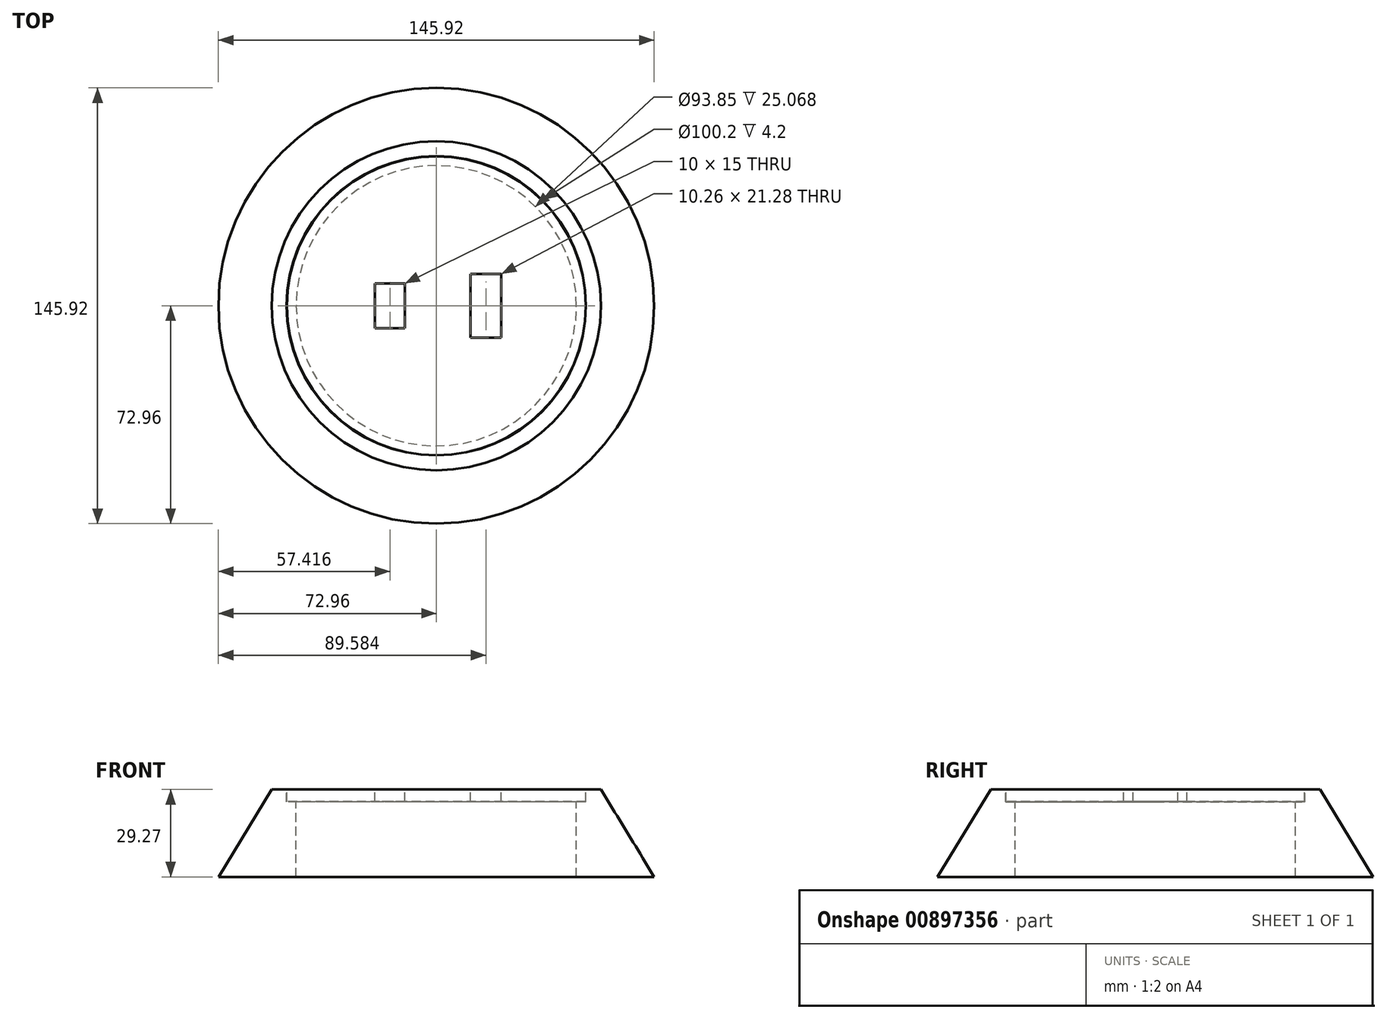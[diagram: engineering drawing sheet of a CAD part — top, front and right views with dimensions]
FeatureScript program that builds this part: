
annotation { "Feature Type Name" : "Feature", "Feature Type Description" : "" }
export const myFeature = defineFeature(function(context is Context, id is Id, definition is map)
    precondition{}
    {
        {
            var Q0;
            Q0=qCreatedBy(makeId("Front.planeOp"),FACE);
            var sketch = newSketch(context, id + "F0", { "sketchPlane" : qUnion([Q0])});
            skLineSegment(sketch, "E0.bottom", {"start": v(0, 29.27) * mm, "end": v(-50, 29.27) * mm});
            skLineSegment(sketch, "E0.top", {"start": v(0, 25.27) * mm, "end": v(-50, 25.27) * mm});
            skLineSegment(sketch, "E0.left", {"start": v(0, 29.27) * mm, "end": v(0, 25.27) * mm});
            skLineSegment(sketch, "E0.right", {"start": v(-50, 29.27) * mm, "end": v(-50, 25.27) * mm});
            skLineSegment(sketch, "E1", {"start": v(-46.93, 0) * mm, "end": v(-72.96, 0) * mm});
            skLineSegment(sketch, "E2", {"start": v(-72.96, 0) * mm, "end": v(-55.1, 29.27) * mm});
            skLineSegment(sketch, "E3", {"start": v(-55.1, 29.27) * mm, "end": v(-50.1, 29.27) * mm});
            skLineSegment(sketch, "E4", {"start": v(-50.1, 29.27) * mm, "end": v(-50.1, 25.07) * mm});
            skLineSegment(sketch, "E5", {"start": v(-50.1, 25.07) * mm, "end": v(-46.93, 25.07) * mm});
            skLineSegment(sketch, "E6", {"start": v(-46.93, 25.07) * mm, "end": v(-46.93, 0) * mm});
            skSolve(sketch);
        }
        {
            var Q0;
            Q0=makeQuery(id+"F0.imprint","IMPRINT",FACE,{"disambiguationData":[TD([[makeQuery(id+"F0.imprint","IMPRINT",EDGE,{"derivedFrom":sQuery(id+"F0.wireOp",EDGE,"E0.bottom")}),1.0]])]});
            var Q1;
            Q1=sQuery(id+"F0.wireOp",EDGE,"E0.left");
            revolve(context, id + "F1", {"surfaceOperationType" : NewSurfaceOperationType.NEW, "entities" : qUnion([Q0]), "axis" : qUnion([Q1]), "revolveType" : RevolveType.FULL});
        }
        {
            var Q0;
            Q0=makeQuery(id+"F0.imprint","IMPRINT",FACE,{"disambiguationData":[TD([[makeQuery(id+"F0.imprint","IMPRINT",EDGE,{"derivedFrom":sQuery(id+"F0.wireOp",EDGE,"E1")}),-1.0]])]});
            var Q1;
            Q1=sQuery(id+"F0.wireOp",EDGE,"E0.left");
            revolve(context, id + "F2", {"surfaceOperationType" : NewSurfaceOperationType.NEW, "entities" : qUnion([Q0]), "axis" : qUnion([Q1]), "revolveType" : RevolveType.FULL});
        }
        {
            var Q0;
            Q0=makeQuery(id+"F1.opRevolve","SWEPT_FACE",FACE,{"disambiguationData":[OSD([sQuery(id+"F0.wireOp",EDGE,"E0.bottom")])]});
            var sketch = newSketch(context, id + "F3", { "sketchPlane" : qUnion([Q0])});
            skLineSegment(sketch, "E7.bottom", {"start": v(-20.54, 7.5) * mm, "end": v(-10.54, 7.5) * mm});
            skLineSegment(sketch, "E7.top", {"start": v(-20.54, -7.5) * mm, "end": v(-10.54, -7.5) * mm});
            skLineSegment(sketch, "E7.left", {"start": v(-20.54, 7.5) * mm, "end": v(-20.54, -7.5) * mm});
            skLineSegment(sketch, "E7.right", {"start": v(-10.54, 7.5) * mm, "end": v(-10.54, -7.5) * mm});
            skLineSegment(sketch, "E8.bottom", {"start": v(21.75, -10.64) * mm, "end": v(11.5, -10.64) * mm});
            skLineSegment(sketch, "E8.top", {"start": v(21.75, 10.64) * mm, "end": v(11.5, 10.64) * mm});
            skLineSegment(sketch, "E8.left", {"start": v(21.75, -10.64) * mm, "end": v(21.75, 10.64) * mm});
            skLineSegment(sketch, "E8.right", {"start": v(11.5, -10.64) * mm, "end": v(11.5, 10.64) * mm});
            skPoint(sketch, "E8.middle", {"position": v(16.62, 0) * mm});
            skSolve(sketch);
        }
        {
            var Q0;
            Q0 = qSketchRegion(id + "F3", true);
            extrude(context, id + "F4", {"entities" : qUnion([Q0]), "operationType" : NewBodyOperationType.REMOVE, "endBound" : BoundingType.UP_TO_NEXT, "oppositeDirection" : true, "depth" : 25 * mm, "offsetDistance" : 25 * mm});
        }
    });
